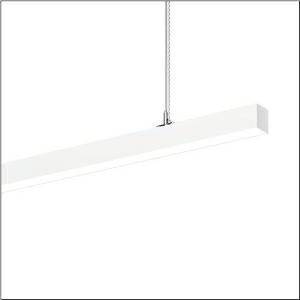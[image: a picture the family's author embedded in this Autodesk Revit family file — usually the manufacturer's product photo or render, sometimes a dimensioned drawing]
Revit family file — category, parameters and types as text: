
# Revit family: silica_21_51mx30dc49wb
name_source: partatom
category: Lighting Fixtures
units: mm (PartAtom-declared; Revit-internal decimal feet)

## family parameters
Cut with Voids When Loaded = No
Host = Face
Light Source = No
Part Type = Normal
Room Calculation Point = No
Round Connector Dimension = Use Diameter
Shared = No

## types (1)
- --- (1 x LED, 10520 lm, 64.1 W, 4000K)
    Apparent Load = 64 VA
    CIE Flux Codes = 47 79 96 57 100
    Color Rendering = 80
    Color Temperature = 4000K
    Default Elevation = 1800 mm
    Description = Silica 21, office luminaire, primary optical cover: cover, of PMMA, opal, light emission: direct/indirect distribution, primary light characteristic: symmetric, installation type: suspended mounting, LED, rated luminous flux: 10.520lm, luminous efficacy: 164lm/W, light colour: 840, colour temperature: 4000K, control gear: DALI 2, with terminal, 3+2-pole, max. 2.5mm², mains connection: 220..240V, AC, 50/60Hz, rated input power: 64.1W, luminaire housing, of aluminium, traffic white (RAL 9016), length: 3.004mm, width: 53mm, height: 53mm, protection rating (complete): IP20, insulation class (complete): insulation class I (protective earthing), certification: CE, permissible operating ambient temperature: 0..+35°C, standard: EN 50419, packaging unit: 1 piece
    Height = 53 mm
    Lamp = 1 x LED
    Lamp Light Flux = 10520 lm
    Lamp Power = 64.1 W
    Lamp count = 1
    Length = 3004 mm
    Luminous efficacy = 164 lm/W
    Manufacturer = Siteco
    ModVariant = No
    Model = 51MX30DC49WB
    Mounting Place = Ceiling
    Mounting Type = Pendant
    Number of Poles = 1
    OnlyDefault = Yes
    Power Factor = 1
    Product Name = Silica 21
    Product group = office luminaire | ceiling pendant
    ProductGroupID = 903
    Protection Class = Protection class I
    Protection Degree = IP 20
    RLX_Detail_Level = 1
    RLX_Emergency_Light_Flux = 0 lm
    RLX_Emergency_Type = 0
    RLX_Emergency_Type_DB = No
    RlxData = <blob elided: 20893 chars, md5=5a6df8f4>
    Socket = socket
    Standby Power = 0 W
    System Light Flux = 10520 lm
    System Power = 64 W
    Type Comments = factory setting: luminous flux: 100 % | dim-lin: 254 | 218 mA
    Type Image = l_1349023.jpg
    URL = http://relux.com
    VarID = @adj_117599
    Voltage = 0 V
    Weight = 0.00 kg
    Width = 53 mm

## geometry (parser evidence)
native form markers: Blend x4, Sweep x12
no freeform markers — native parametric forms only
